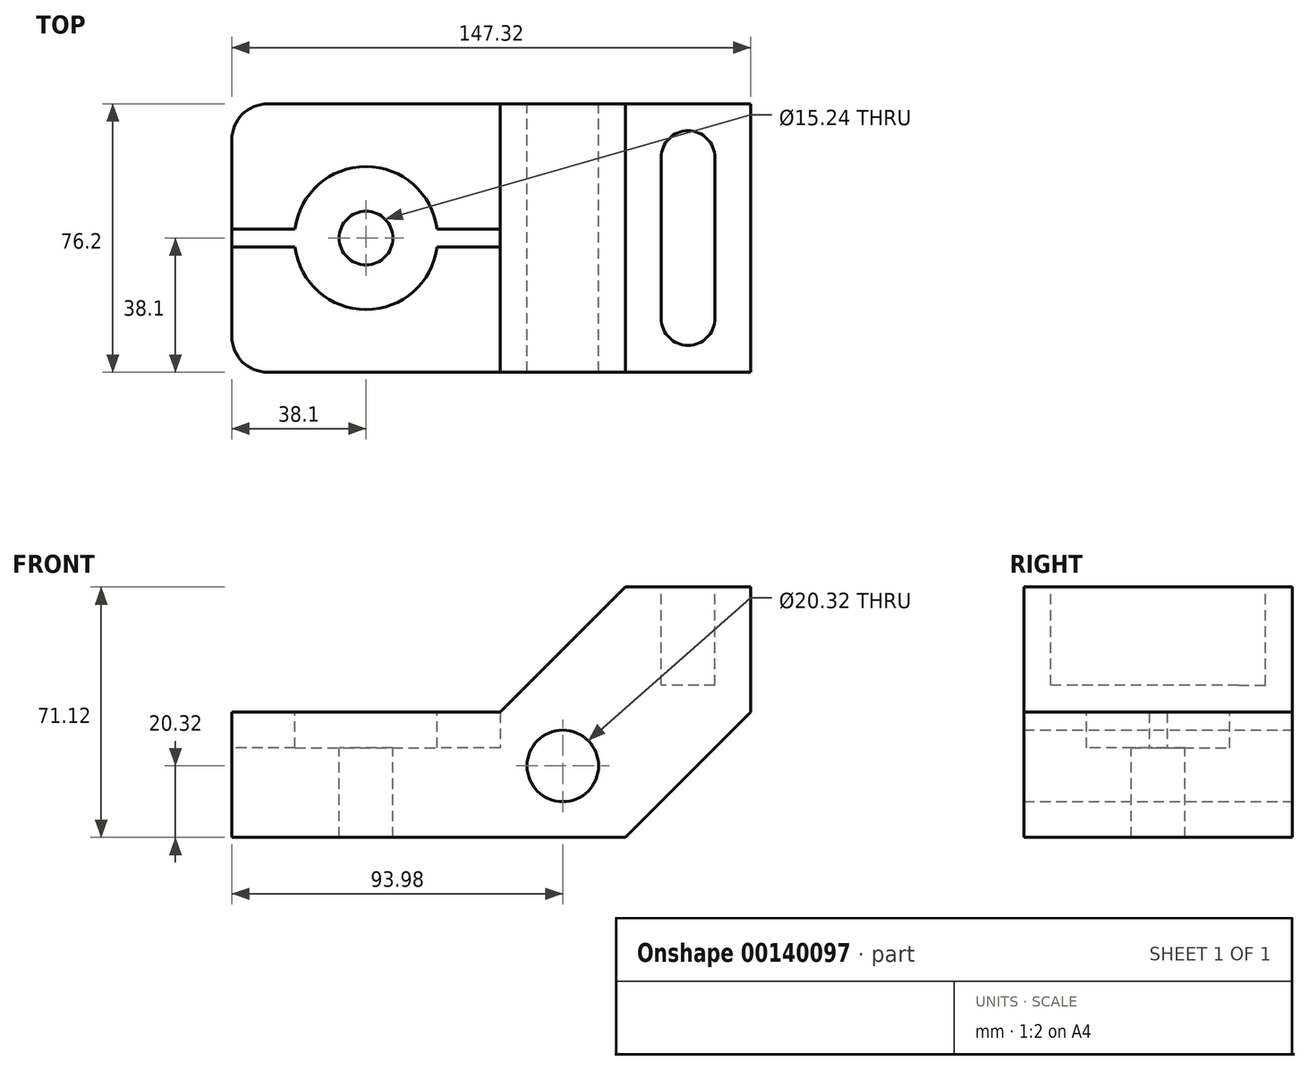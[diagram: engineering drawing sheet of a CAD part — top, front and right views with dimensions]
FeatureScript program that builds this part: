
annotation { "Feature Type Name" : "Feature", "Feature Type Description" : "" }
export const myFeature = defineFeature(function(context is Context, id is Id, definition is map)
    precondition{}
    {
        {
            var Q0;
            Q0=qCreatedBy(makeId("Front.planeOp"),FACE);
            var sketch = newSketch(context, id + "F0", { "sketchPlane" : qUnion([Q0])});
            skLineSegment(sketch, "E0", {"start": v(0, 0) * mm, "end": v(111.76, 0) * mm});
            skLineSegment(sketch, "E1", {"start": v(111.76, 0) * mm, "end": v(147.32, 35.56) * mm});
            skLineSegment(sketch, "E2", {"start": v(147.32, 35.56) * mm, "end": v(147.32, 71.12) * mm});
            skLineSegment(sketch, "E3", {"start": v(147.32, 71.12) * mm, "end": v(111.76, 71.12) * mm});
            skLineSegment(sketch, "E4", {"start": v(111.76, 71.12) * mm, "end": v(76.2, 35.56) * mm});
            skLineSegment(sketch, "E5", {"start": v(76.2, 35.56) * mm, "end": v(0, 35.56) * mm});
            skLineSegment(sketch, "E6", {"start": v(0, 35.56) * mm, "end": v(0, 0) * mm});
            skCircle(sketch, "E7", {"center": v(93.98, 20.32) * mm, "radius": 10.16 * mm});
            skSolve(sketch);
        }
        {
            var Q0;
            Q0=makeQuery(id+"F0.imprint","IMPRINT",FACE,{"disambiguationData":[TD([[makeQuery(id+"F0.imprint","IMPRINT",EDGE,{"derivedFrom":sQuery(id+"F0.wireOp",EDGE,"E0")}),1.0]])]});
            extrude(context, id + "F1", {"entities" : qUnion([Q0]), "endBound" : BoundingType.SYMMETRIC, "depth" : 76.2 * mm});
        }
        {
            var Q0;
            Q0=makeQuery(id+"F1.opExtrude","SWEPT_FACE",FACE,{"disambiguationData":[OSD([sQuery(id+"F0.wireOp",EDGE,"E3")])]});
            var sketch = newSketch(context, id + "F2", { "sketchPlane" : qUnion([Q0])});
            skLineSegment(sketch, "E8", {"start": v(121.92, 22.86) * mm, "end": v(121.92, -22.86) * mm});
            skLineSegment(sketch, "E9", {"start": v(137.16, 22.86) * mm, "end": v(137.16, -22.86) * mm});
            skArc(sketch, "E10", {"start": v(121.92, 22.86) * mm, "mid": v(129.54, 30.48) * mm, "end": v(137.16, 22.86) * mm});
            skArc(sketch, "E11", {"start": v(121.92, -22.86) * mm, "mid": v(129.54, -30.48) * mm, "end": v(137.16, -22.86) * mm});
            skSolve(sketch);
        }
        {
            var Q0;
            Q0=makeQuery(id+"F2.imprint","IMPRINT",FACE,{"disambiguationData":[TD([[makeQuery(id+"F2.imprint","IMPRINT",EDGE,{"derivedFrom":sQuery(id+"F2.wireOp",EDGE,"E8")}),1.0]])]});
            extrude(context, id + "F3", {"entities" : qUnion([Q0]), "operationType" : NewBodyOperationType.REMOVE, "oppositeDirection" : true, "depth" : 27.94 * mm});
        }
        {
            var Q0;
            Q0=makeQuery(id+"F1.opExtrude","SWEPT_FACE",FACE,{"disambiguationData":[OSD([sQuery(id+"F0.wireOp",EDGE,"E5")])]});
            var sketch = newSketch(context, id + "F4", { "sketchPlane" : qUnion([Q0])});
            skPoint(sketch, "E12", {"position": v(38.1, 0) * mm});
            skPoint(sketch, "E12.positionSnap0", {"position": v(0, 0) * mm});
            skSolve(sketch);
        }
        {
            var Q0;
            Q0=sQuery(id+"F4.wireOp",VERTEX,"E12");
            var Q1;
            Q1=makeQuery(id+"F1.opExtrude","SWEPT_BODY",BODY,{"disambiguationData":[OSD([sQuery(id+"F0.wireOp",EDGE,"E0"),sQuery(id+"F0.wireOp",EDGE,"E1"),sQuery(id+"F0.wireOp",EDGE,"E2"),sQuery(id+"F0.wireOp",EDGE,"E3"),sQuery(id+"F0.wireOp",EDGE,"E4"),sQuery(id+"F0.wireOp",EDGE,"E5"),sQuery(id+"F0.wireOp",EDGE,"E6"),sQuery(id+"F0.wireOp",EDGE,"E7")])]});
            hole(context, id + "F5", {"style" : HoleStyle.C_BORE, "endStyle" : HoleEndStyle.THROUGH, "holeDiameter" : 15.24 * mm, "cBoreDiameter" : 40.64 * mm, "cBoreDepth" : 10.16 * mm, "locations" : qUnion([Q0]), "scope" : qUnion([Q1]), "isTappedThrough" : true});
        }
        {
            var Q0;
            Q0=makeQuery(id+"F1.opExtrude","SWEPT_FACE",FACE,{"disambiguationData":[OSD([sQuery(id+"F0.wireOp",EDGE,"E6")])]});
            var sketch = newSketch(context, id + "F6", { "sketchPlane" : qUnion([Q0])});
            skLineSegment(sketch, "E13", {"start": v(0, -28.21) * mm, "end": v(0, 118.42) * mm, "construction": true});
            skLineSegment(sketch, "E14.bottom", {"start": v(-2.54, 35.56) * mm, "end": v(2.54, 35.56) * mm});
            skLineSegment(sketch, "E14.top", {"start": v(-2.54, 25.4) * mm, "end": v(2.54, 25.4) * mm});
            skLineSegment(sketch, "E14.left", {"start": v(-2.54, 35.56) * mm, "end": v(-2.54, 25.4) * mm});
            skLineSegment(sketch, "E14.right", {"start": v(2.54, 35.56) * mm, "end": v(2.54, 25.4) * mm});
            skSolve(sketch);
        }
        {
            var Q0;
            Q0=makeQuery(id+"F6.imprint","IMPRINT",FACE,{"disambiguationData":[TD([[makeQuery(id+"F6.imprint","IMPRINT",EDGE,{"derivedFrom":sQuery(id+"F6.wireOp",EDGE,"E14.bottom")}),1.0]])]});
            extrude(context, id + "F7", {"entities" : qUnion([Q0]), "operationType" : NewBodyOperationType.REMOVE, "oppositeDirection" : true, "depth" : 76.2 * mm});
        }
        {
            var Q0;
            Q0=makeQuery(id+"F1.opExtrude","CAP_EDGE",EDGE,{"disambiguationData":[OSD([sQuery(id+"F0.wireOp",EDGE,"E6")])],"isStart":false});
            var Q1;
            Q1=makeQuery(id+"F1.opExtrude","CAP_EDGE",EDGE,{"disambiguationData":[OSD([sQuery(id+"F0.wireOp",EDGE,"E6")])],"isStart":true});
            fillet(context, id + "F8", {"entities" : qUnion([Q0, Q1]), "radius" : 10.16 * mm, "tangentPropagation" : true, "allowEdgeOverflow" : false});
        }
    });
